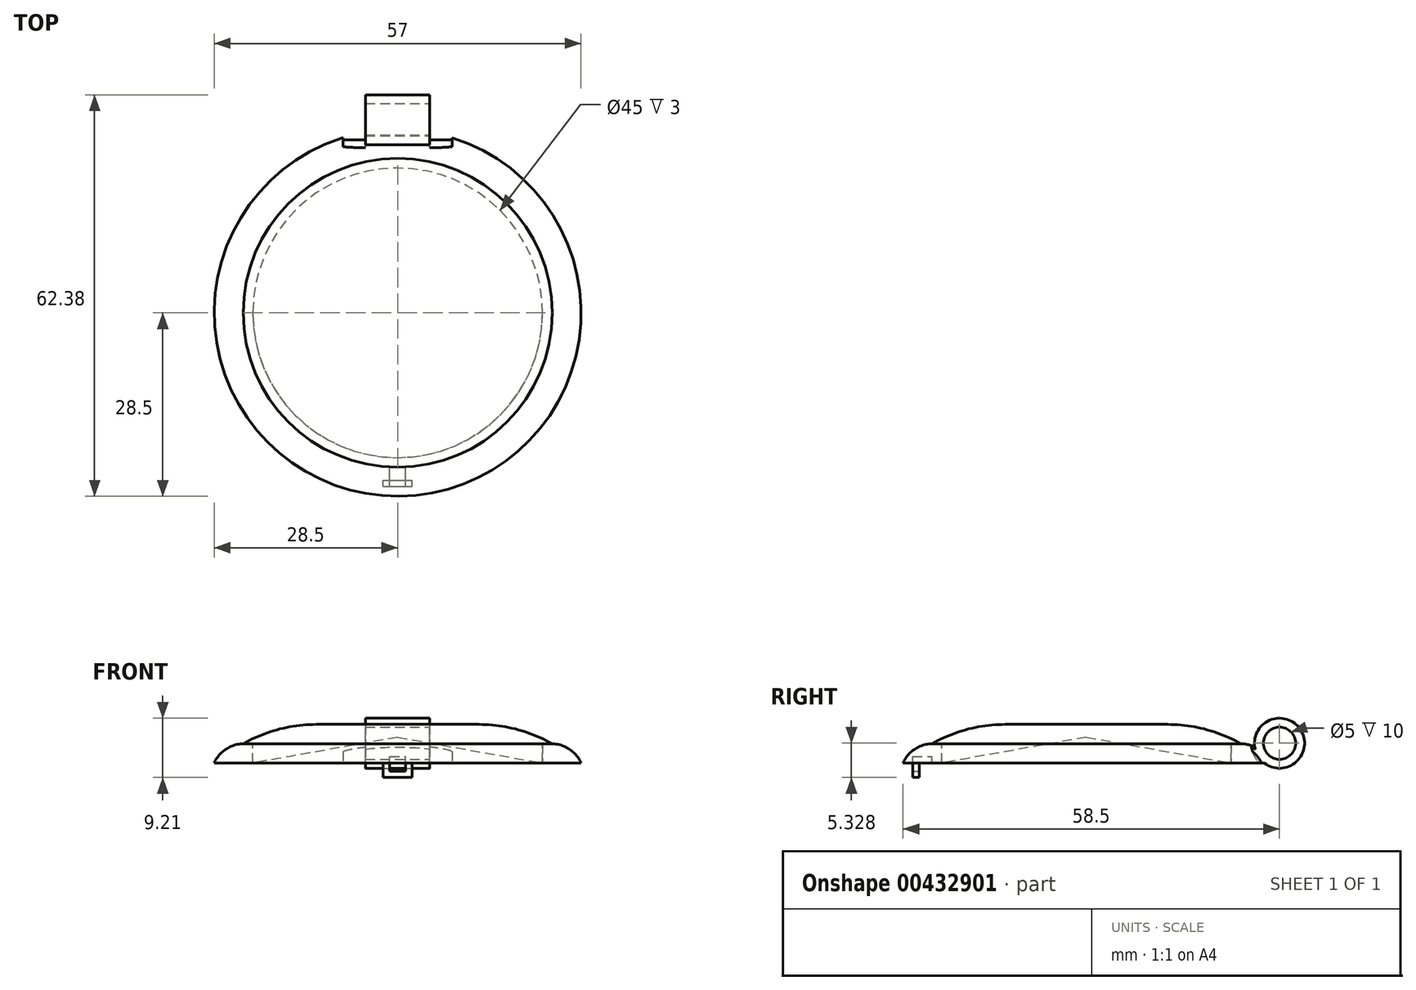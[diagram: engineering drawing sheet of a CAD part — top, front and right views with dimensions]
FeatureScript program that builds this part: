
annotation { "Feature Type Name" : "Feature", "Feature Type Description" : "" }
export const myFeature = defineFeature(function(context is Context, id is Id, definition is map)
    precondition{}
    {
        {
            var Q0;
            Q0=qCreatedBy(makeId("Top.planeOp"),FACE);
            var sketch = newSketch(context, id + "F0", { "sketchPlane" : qUnion([Q0])});
            skCircle(sketch, "E0", {"center": v(0, 0) * mm, "radius": 28.5 * mm});
            skCircle(sketch, "E1", {"center": v(0, 0) * mm, "radius": 22.5 * mm});
            skSolve(sketch);
        }
        {
            var Q0;
            Q0=makeQuery(id+"F0.imprint","IMPRINT",FACE,{"disambiguationData":[TD([[makeQuery(id+"F0.imprint","IMPRINT",EDGE,{"derivedFrom":sQuery(id+"F0.wireOp",EDGE,"E0")}),1.0]])]});
            extrude(context, id + "F1", {"entities" : qUnion([Q0]), "depth" : 3 * mm});
        }
        {
            var Q0;
            Q0=makeQuery(id+"F1.opExtrude","CAP_EDGE",EDGE,{"disambiguationData":[OSD([sQuery(id+"F0.wireOp",EDGE,"E0")])],"isStart":false});
            fillet(context, id + "F2", {"entities" : qUnion([Q0]), "radius" : 5 * mm, "tangentPropagation" : true, "allowEdgeOverflow" : false});
        }
        {
            var Q0;
            Q0=makeQuery(id+"F1.opExtrude","SWEPT_BODY",BODY,{"disambiguationData":[OSD([sQuery(id+"F0.wireOp",EDGE,"E0"),sQuery(id+"F0.wireOp",EDGE,"E1")])]});
            var Q1;
            Q1=makeQuery(id+"F2.opFillet","BLEND_FACE",FACE,{"disambiguationData":[OSD([sQuery(id+"F0.wireOp",EDGE,"E0")])]});
            transform(context, id + "F3", {"entities" : qUnion([Q0]), "transformType" : TransformType.ROTATION, "transformAxis" : qUnion([Q1]), "angle" : 90 * degree, "oppositeDirection" : true, "makeCopy" : false});
        }
        {
            var Q0;
            Q0=qCreatedBy(makeId("Front.planeOp"),FACE);
            var sketch = newSketch(context, id + "F4", { "sketchPlane" : qUnion([Q0])});
            skLineSegment(sketch, "E2.top", {"start": v(0, 6) * mm, "end": v(-22.5, 6) * mm});
            skLineSegment(sketch, "E2.right", {"start": v(-22.5, 0) * mm, "end": v(-22.5, 6) * mm});
            skLineSegment(sketch, "E3", {"start": v(-22.5, 3) * mm, "end": v(0, 4) * mm});
            skLineSegment(sketch, "E4.bottom", {"start": v(-22.5, 3) * mm, "end": v(-24, 3) * mm});
            skLineSegment(sketch, "E4.top", {"start": v(-22.5, 6) * mm, "end": v(-24, 6) * mm});
            skLineSegment(sketch, "E4.left", {"start": v(-22.5, 3) * mm, "end": v(-22.5, 6) * mm});
            skLineSegment(sketch, "E4.right", {"start": v(-24, 3) * mm, "end": v(-24, 6) * mm});
            skLineSegment(sketch, "E5", {"start": v(0, 6) * mm, "end": v(0, 4) * mm});
            skLineSegment(sketch, "E6", {"start": v(-22.5, 0) * mm, "end": v(0, 4) * mm});
            skLineSegment(sketch, "E7.right", {"start": v(-1.25, -1.25) * mm, "end": v(-1.25, 0) * mm});
            skLineSegment(sketch, "E8.MirrorCS", {"start": v(1.25, -1.25) * mm, "end": v(1.25, 0) * mm});
            skLineSegment(sketch, "E9", {"start": v(-1.25, 0) * mm, "end": v(1.25, 0) * mm});
            skLineSegment(sketch, "E10", {"start": v(-1.25, -1.25) * mm, "end": v(1.25, -1.25) * mm});
            skLineSegment(sketch, "E11.bottom", {"start": v(-2.25, 0) * mm, "end": v(2.25, 0) * mm});
            skLineSegment(sketch, "E11.top", {"start": v(-2.25, -2.25) * mm, "end": v(2.25, -2.25) * mm});
            skLineSegment(sketch, "E11.left", {"start": v(-2.25, 0) * mm, "end": v(-2.25, -2.25) * mm});
            skLineSegment(sketch, "E11.right", {"start": v(2.25, 0) * mm, "end": v(2.25, -2.25) * mm});
            skLineSegment(sketch, "E12.top", {"start": v(-1.25, 1) * mm, "end": v(1.25, 1) * mm});
            skLineSegment(sketch, "E12.left", {"start": v(-1.25, 0) * mm, "end": v(-1.25, 1) * mm});
            skLineSegment(sketch, "E12.right", {"start": v(1.25, 0) * mm, "end": v(1.25, 1) * mm});
            skSolve(sketch);
        }
        {
            var Q0;
            Q0=makeQuery(id+"F4.imprint","IMPRINT",FACE,{"disambiguationData":[TD([[makeQuery(id+"F4.imprint","IMPRINT",EDGE,{"derivedFrom":sQuery(id+"F4.wireOp",EDGE,"E2.top")}),1.0]])]});
            var Q1;
            Q1=makeQuery(id+"F4.imprint","IMPRINT",FACE,{"disambiguationData":[TD([[makeQuery(id+"F4.imprint","IMPRINT",EDGE,{"derivedFrom":sQuery(id+"F4.wireOp",EDGE,"E4.bottom")}),-1.0]])]});
            var Q2;
            Q2=makeQuery(id+"F4.imprint","IMPRINT",FACE,{"disambiguationData":[TD([[makeQuery(id+"F4.imprint","IMPRINT",EDGE,{"derivedFrom":sQuery(id+"F4.wireOp",EDGE,"E2.right")}),-1.0]])]});
            var Q3;
            Q3=sQuery(id+"F4.wireOp",EDGE,"E5");
            revolve(context, id + "F5", {"entities" : qUnion([Q0, Q1, Q2]), "axis" : qUnion([Q3]), "revolveType" : RevolveType.FULL});
        }
        {
            var Q0;
            Q0=makeQuery(id+"F5.opRevolve","SWEPT_EDGE",EDGE,{"disambiguationData":[OSD([sQuery(id+"F4.wireOp",EDGE,"E4.top"),sQuery(id+"F4.wireOp",EDGE,"E4.right")])]});
            fillet(context, id + "F6", {"entities" : qUnion([Q0]), "radius" : 23 * mm, "tangentPropagation" : true, "allowEdgeOverflow" : false});
        }
        {
            var Q0;
            {var subQ1=sQuery(id+"F4.wireOp",EDGE,"E7.right");Q0=makeQuery(id+"F4.imprint","IMPRINT",FACE,{"disambiguationData":[TD([[makeQuery(id+"F4.imprint","IMPRINT",EDGE,{"derivedFrom":subQ1}),1.0]])]});}
            extrude(context, id + "F7", {"entities" : qUnion([Q0]), "operationType" : NewBodyOperationType.ADD, "depth" : 27 * mm, "hasSecondDirection" : true, "secondDirectionOppositeDirection" : false, "secondDirectionDepth" : 26 * mm});
        }
        {
            var Q0;
            Q0=qCreatedBy(makeId("Right.planeOp"),FACE);
            var sketch = newSketch(context, id + "F8", { "sketchPlane" : qUnion([Q0])});
            skCircle(sketch, "E13", {"center": v(30, 3.08) * mm, "radius": 2.5 * mm});
            skCircle(sketch, "E14", {"center": v(30, 3.08) * mm, "radius": 3.88 * mm});
            skCircle(sketch, "E15", {"center": v(30, 3.08) * mm, "radius": 4.38 * mm});
            skSolve(sketch);
        }
        {
            var Q0;
            Q0=makeQuery(id+"F8.imprint","IMPRINT",FACE,{"disambiguationData":[TD([[makeQuery(id+"F8.imprint","IMPRINT",EDGE,{"derivedFrom":sQuery(id+"F8.wireOp",EDGE,"E13")}),-1.0]])]});
            extrude(context, id + "F9", {"entities" : qUnion([Q0]), "operationType" : NewBodyOperationType.ADD, "endBound" : BoundingType.SYMMETRIC, "oppositeDirection" : true, "depth" : 10 * mm, "hasSecondDirection" : true, "secondDirectionOppositeDirection" : true, "secondDirectionDepth" : 12 * mm});
        }
        {
            var Q0;
            Q0=makeQuery(id+"F8.imprint","IMPRINT",FACE,{"disambiguationData":[TD([[makeQuery(id+"F8.imprint","IMPRINT",EDGE,{"derivedFrom":sQuery(id+"F8.wireOp",EDGE,"E14")}),-1.0]])]});
            var Q1;
            Q1=makeQuery(id+"F8.imprint","IMPRINT",FACE,{"disambiguationData":[TD([[makeQuery(id+"F8.imprint","IMPRINT",EDGE,{"derivedFrom":sQuery(id+"F8.wireOp",EDGE,"E13")}),-1.0]])]});
            extrude(context, id + "F10", {"entities" : qUnion([Q0, Q1]), "operationType" : NewBodyOperationType.REMOVE, "oppositeDirection" : true, "depth" : 8.5 * mm, "hasSecondDirection" : true, "secondDirectionOppositeDirection" : true, "secondDirectionDepth" : 5 * mm});
        }
        {
            var Q0;
            Q0=makeQuery(id+"F8.imprint","IMPRINT",FACE,{"disambiguationData":[TD([[makeQuery(id+"F8.imprint","IMPRINT",EDGE,{"derivedFrom":sQuery(id+"F8.wireOp",EDGE,"E14")}),-1.0]])]});
            var Q1;
            Q1=makeQuery(id+"F8.imprint","IMPRINT",FACE,{"disambiguationData":[TD([[makeQuery(id+"F8.imprint","IMPRINT",EDGE,{"derivedFrom":sQuery(id+"F8.wireOp",EDGE,"E13")}),-1.0]])]});
            extrude(context, id + "F11", {"entities" : qUnion([Q0, Q1]), "operationType" : NewBodyOperationType.REMOVE, "depth" : 8.5 * mm, "hasSecondDirection" : true, "secondDirectionOppositeDirection" : false, "secondDirectionDepth" : 5 * mm});
        }
        {
            var Q0;
            Q0=makeQuery(id+"F4.imprint","IMPRINT",FACE,{"disambiguationData":[TD([[makeQuery(id+"F4.imprint","IMPRINT",EDGE,{"derivedFrom":sQuery(id+"F4.wireOp",EDGE,"E9")}),1.0]])]});
            extrude(context, id + "F12", {"entities" : qUnion([Q0]), "operationType" : NewBodyOperationType.REMOVE, "depth" : 27 * mm, "hasSecondDirection" : true, "secondDirectionOppositeDirection" : false, "secondDirectionDepth" : 24 * mm});
        }
    });
